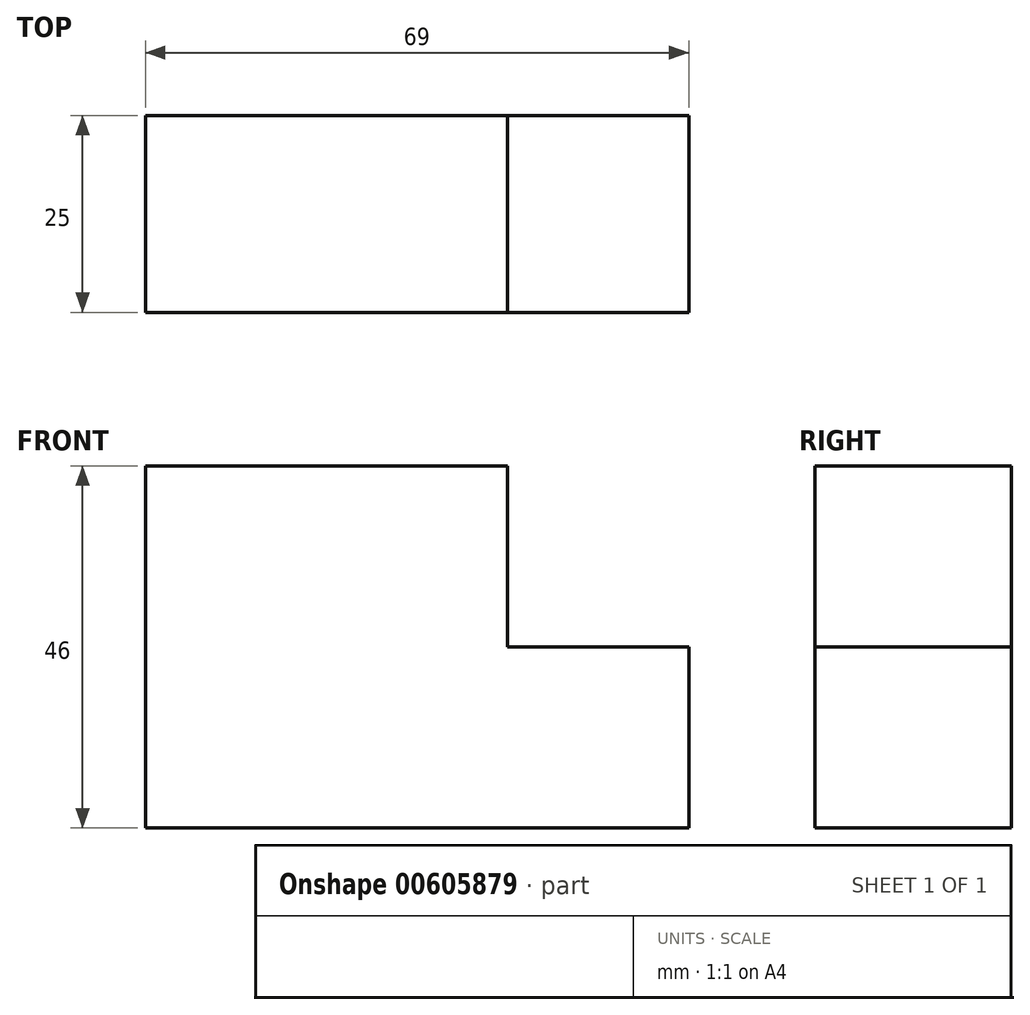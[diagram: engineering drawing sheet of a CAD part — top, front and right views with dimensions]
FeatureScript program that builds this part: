
annotation { "Feature Type Name" : "Feature", "Feature Type Description" : "" }
export const myFeature = defineFeature(function(context is Context, id is Id, definition is map)
    precondition{}
    {
        {
            var Q0;
            Q0=qCreatedBy(makeId("Front.planeOp"),FACE);
            var sketch = newSketch(context, id + "F0", { "sketchPlane" : qUnion([Q0])});
            skLineSegment(sketch, "E0", {"start": v(0, 23) * mm, "end": v(-23, 23) * mm});
            skLineSegment(sketch, "E1", {"start": v(-23, 23) * mm, "end": v(-23, -23) * mm});
            skLineSegment(sketch, "E2", {"start": v(-23, -23) * mm, "end": v(45, -23) * mm});
            skLineSegment(sketch, "E3", {"start": v(0, 23) * mm, "end": v(23, 23) * mm});
            skLineSegment(sketch, "E4", {"start": v(23, 23) * mm, "end": v(23, 0) * mm});
            skLineSegment(sketch, "E5", {"start": v(23, 0) * mm, "end": v(46, 0) * mm});
            skLineSegment(sketch, "E6", {"start": v(46, 0) * mm, "end": v(46, -23) * mm});
            skLineSegment(sketch, "E7", {"start": v(-23, 23) * mm, "end": v(23, 23) * mm});
            skLineSegment(sketch, "E8", {"start": v(46, -23) * mm, "end": v(-23, -23) * mm});
            skLineSegment(sketch, "E9", {"start": v(-23, -23) * mm, "end": v(-23, 23) * mm});
            skSolve(sketch);
        }
        {
            var Q0;
            Q0 = qSketchRegion(id + "F0", true);
            extrude(context, id + "F1", {"entities" : qUnion([Q0]), "depth" : 25 * mm, "offsetDistance" : 25 * mm});
        }
    });
